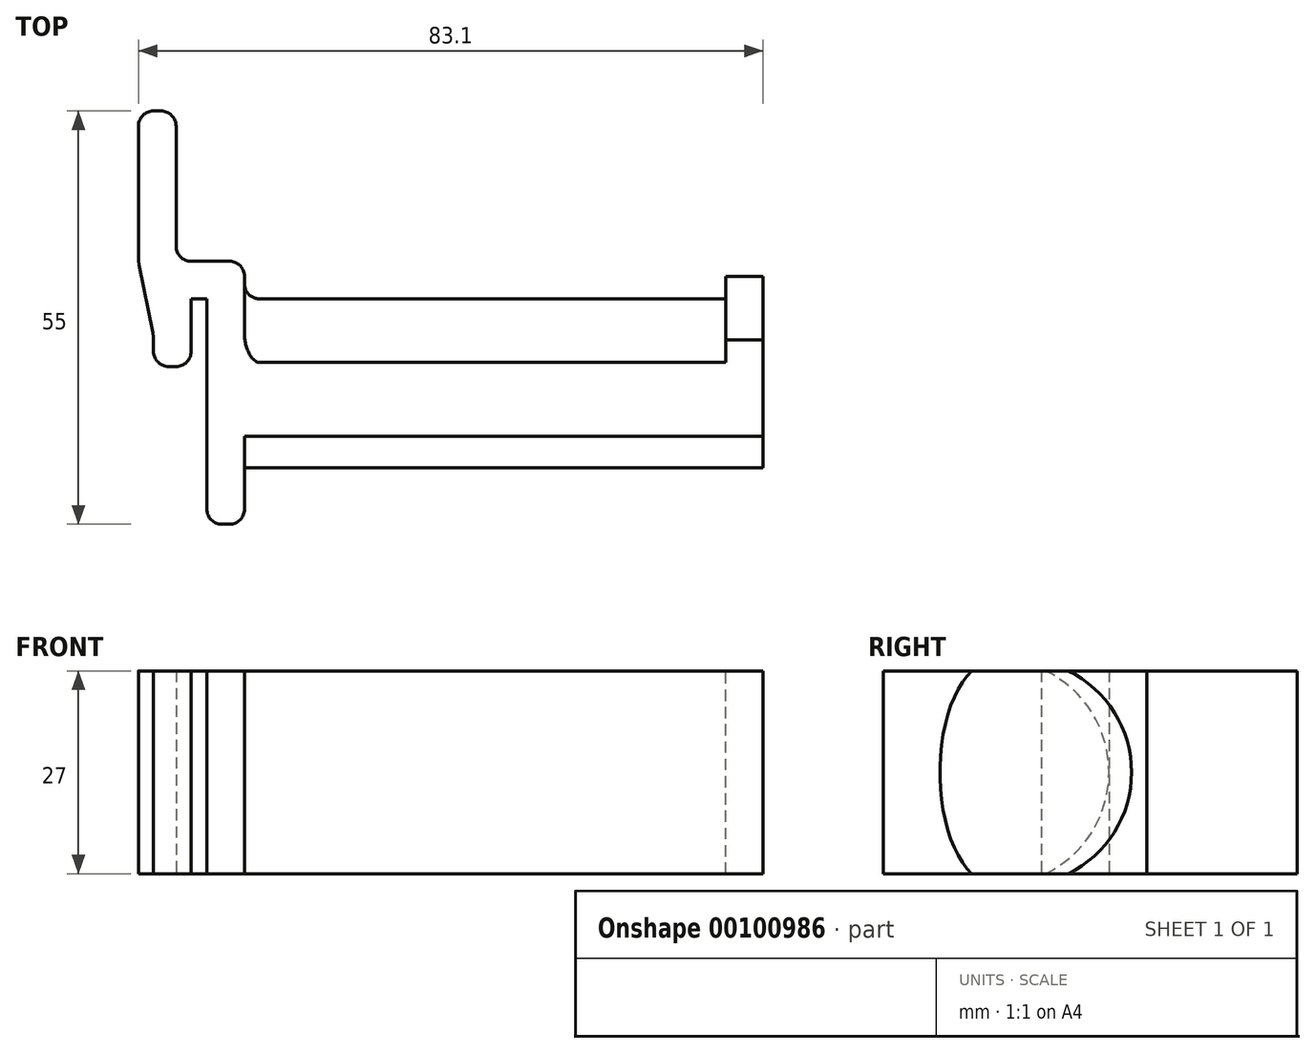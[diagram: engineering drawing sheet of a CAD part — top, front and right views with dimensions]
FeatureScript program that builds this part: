
annotation { "Feature Type Name" : "Feature", "Feature Type Description" : "" }
export const myFeature = defineFeature(function(context is Context, id is Id, definition is map)
    precondition{}
    {
        {
            assignVariable(context, id + "F0", {"name" : "Diameter", "anyValue" : 30});
        }
        {
            assignVariable(context, id + "F1", {"name" : "Width", "anyValue" : 62});
        }
        {
            var Q0;
            Q0=qCreatedBy(makeId("Top.planeOp"),FACE);
            var sketch = newSketch(context, id + "F2", { "sketchPlane" : qUnion([Q0])});
            skLineSegment(sketch, "E0", {"start": v(-10.1, -14) * mm, "end": v(-9.1, -14) * mm});
            skLineSegment(sketch, "E1", {"start": v(-7.1, -12) * mm, "end": v(-7.1, -5) * mm});
            skLineSegment(sketch, "E2", {"start": v(-7.1, -5) * mm, "end": v(-5, -5) * mm});
            skLineSegment(sketch, "E3", {"start": v(-5, -5) * mm, "end": v(-5, -33) * mm});
            skLineSegment(sketch, "E4", {"start": v(-3, -35) * mm, "end": v(-2, -35) * mm});
            skLineSegment(sketch, "E5", {"start": v(0, -33) * mm, "end": v(0, -2) * mm});
            skLineSegment(sketch, "E6", {"start": v(-2, 0) * mm, "end": v(-7.1, 0) * mm});
            skLineSegment(sketch, "E7", {"start": v(-9.1, 2) * mm, "end": v(-9.1, 18) * mm});
            skLineSegment(sketch, "E8", {"start": v(-11.1, 20) * mm, "end": v(-12.1, 20) * mm});
            skLineSegment(sketch, "E9", {"start": v(-14.1, 18) * mm, "end": v(-14.1, 0.5) * mm});
            skLineSegment(sketch, "E10", {"start": v(-12.1, -10.5) * mm, "end": v(-12.1, -12) * mm});
            skPoint(sketch, "E11.visualSharp", {"position": v(-9.1, 0) * mm});
            skArc(sketch, "E11.filletArc", {"start": v(-9.1, 2) * mm, "mid": v(-8.51, 0.59) * mm, "end": v(-7.1, 0) * mm});
            skPoint(sketch, "E12.visualSharp", {"position": v(0, 0) * mm});
            skArc(sketch, "E12.filletArc", {"start": v(0, -2) * mm, "mid": v(-0.59, -0.59) * mm, "end": v(-2, 0) * mm});
            skPoint(sketch, "E13.visualSharp", {"position": v(-9.1, 20) * mm});
            skArc(sketch, "E13.filletArc", {"start": v(-9.1, 18) * mm, "mid": v(-9.69, 19.41) * mm, "end": v(-11.1, 20) * mm});
            skPoint(sketch, "E14.visualSharp", {"position": v(-14.1, 20) * mm});
            skArc(sketch, "E14.filletArc", {"start": v(-12.1, 20) * mm, "mid": v(-13.51, 19.41) * mm, "end": v(-14.1, 18) * mm});
            skPoint(sketch, "E15.visualSharp", {"position": v(0, -35) * mm});
            skArc(sketch, "E15.filletArc", {"start": v(-2, -35) * mm, "mid": v(-0.59, -34.41) * mm, "end": v(0, -33) * mm});
            skPoint(sketch, "E16.visualSharp", {"position": v(-5, -35) * mm});
            skArc(sketch, "E16.filletArc", {"start": v(-5, -33) * mm, "mid": v(-4.41, -34.41) * mm, "end": v(-3, -35) * mm});
            skPoint(sketch, "E17.visualSharp", {"position": v(-7.1, -14) * mm});
            skArc(sketch, "E17.filletArc", {"start": v(-9.1, -14) * mm, "mid": v(-7.69, -13.41) * mm, "end": v(-7.1, -12) * mm});
            skPoint(sketch, "E18.visualSharp", {"position": v(-12.1, -14) * mm});
            skArc(sketch, "E18.filletArc", {"start": v(-12.1, -12) * mm, "mid": v(-11.51, -13.41) * mm, "end": v(-10.1, -14) * mm});
            skLineSegment(sketch, "E19", {"start": v(-14, -0.49) * mm, "end": v(-12.2, -9.51) * mm});
            skPoint(sketch, "E20", {"position": v(-13.1, -5) * mm});
            skPoint(sketch, "E21.visualSharp", {"position": v(-14.1, 0) * mm});
            skArc(sketch, "E21.filletArc", {"start": v(-14.1, 0.5) * mm, "mid": v(-14.08, 0) * mm, "end": v(-14, -0.49) * mm});
            skPoint(sketch, "E22.visualSharp", {"position": v(-12.1, -10) * mm});
            skArc(sketch, "E22.filletArc", {"start": v(-12.1, -10.5) * mm, "mid": v(-12.12, -10) * mm, "end": v(-12.2, -9.51) * mm});
            skSolve(sketch);
        }
        {
            var Q0;
            Q0=qSketchRegion(id+"F2",true);
            extrude(context, id + "F3", {"entities" : qUnion([Q0]), "endBound" : BoundingType.SYMMETRIC, "depth" : (getVariable(context, 'Diameter') * 0.9) * mm});
        }
        {
            var Q0;
            Q0=makeQuery(id+"F3.opExtrude","SWEPT_FACE",FACE,{"disambiguationData":[OSD([sQuery(id+"F2.wireOp",EDGE,"E5")])]});
            var sketch = newSketch(context, id + "F4", { "sketchPlane" : qUnion([Q0])});
            skArc(sketch, "E23", {"start": v(-13.46, -13.5) * mm, "mid": v(-5, 0) * mm, "end": v(-13.46, 13.5) * mm});
            skEllipse(sketch, "E24", {"center": v(-20, 0) * mm, "majorRadius": 15 * mm, "minorRadius": 7.5 * mm, "majorAxis": v(0, -1)});
            skLineSegment(sketch, "E25", {"start": v(-13.46, 13.5) * mm, "end": v(-23.27, 13.5) * mm});
            skLineSegment(sketch, "E26", {"start": v(-13.46, -13.5) * mm, "end": v(-23.27, -13.5) * mm});
            skSolve(sketch);
        }
        {
            var Q0;
            {var subQ0=sQuery(id+"F4.wireOp",EDGE,"E25");var subQ1=sQuery(id+"F4.wireOp",EDGE,"E24");var subQ2=makeQuery(id+"F4.imprint","INTERSECT",VERTEX,{"derivedFrom":[subQ1,subQ0]});Q0=makeQuery(id+"F4.imprint","IMPRINT",FACE,{"disambiguationData":[TD([[makeQuery(id+"F4.imprint","IMPRINT",EDGE,{"disambiguationData":[TD([[subQ2,1.0]])],"derivedFrom":subQ1}),1.0]])]});}
            var Q1;
            {var subQ0=sQuery(id+"F4.wireOp",EDGE,"E23");Q1=makeQuery(id+"F4.imprint","IMPRINT",FACE,{"disambiguationData":[TD([[makeQuery(id+"F4.imprint","IMPRINT",EDGE,{"derivedFrom":subQ0}),1.0]])]});}
            extrude(context, id + "F5", {"entities" : qUnion([Q0, Q1]), "operationType" : NewBodyOperationType.ADD, "depth" : (getVariable(context, 'Width') + 7) * mm});
        }
        {
            var Q0;
            Q0=makeQuery(id+"F5.opExtrude","CAP_FACE",FACE,{"disambiguationData":[OSD([sQuery(id+"F4.wireOp",EDGE,"E23"),sQuery(id+"F4.wireOp",EDGE,"E24"),sQuery(id+"F4.wireOp",EDGE,"E25"),sQuery(id+"F4.wireOp",EDGE,"E26")])],"isStart":false});
            var sketch = newSketch(context, id + "F6", { "sketchPlane" : qUnion([Q0])});
            skLineSegment(sketch, "E27.0", {"start": v(-13.46, 13.5) * mm, "end": v(-2, 13.5) * mm});
            skLineSegment(sketch, "E28.0", {"start": v(-13.46, -13.5) * mm, "end": v(-2, -13.5) * mm});
            skArc(sketch, "E29", {"start": v(-10.46, -13.5) * mm, "mid": v(-2, 0) * mm, "end": v(-10.46, 13.5) * mm});
            skPoint(sketch, "E30", {"position": v(-20, 0) * mm});
            skSolve(sketch);
        }
        {
            var Q0;
            Q0=qSketchRegion(id+"F6",true);
            var Q1;
            {var subQ2=sQuery(id+"F6.wireOp",EDGE,"E29");Q1=makeQuery(id+"F6.imprint","IMPRINT",FACE,{"disambiguationData":[TD([[makeQuery(id+"F6.imprint","IMPRINT",EDGE,{"derivedFrom":subQ2}),1.0]])]});}
            extrude(context, id + "F7", {"entities" : qUnion([Q0, Q1]), "operationType" : NewBodyOperationType.ADD, "oppositeDirection" : true, "depth" : 5 * mm});
        }
        {
            var Q0;
            Q0=makeQuery(id+"F5.opExtrude","CAP_EDGE",EDGE,{"disambiguationData":[OSD([sQuery(id+"F4.wireOp",EDGE,"E23")])],"isStart":true});
            var Q1;
            Q1=makeQuery(id+"F5.opExtrude","CAP_EDGE",EDGE,{"disambiguationData":[OSD([sQuery(id+"F4.wireOp",EDGE,"E24")])],"isStart":true});
            var Q2;
            Q2=makeQuery(id+"F7.opExtrude","CAP_EDGE",EDGE,{"disambiguationData":[OSD([sQuery(id+"F4.wireOp",EDGE,"E23")])],"isStart":false});
            fillet(context, id + "F8", {"entities" : qUnion([Q0, Q1, Q2]), "radius" : 2 * mm, "tangentPropagation" : true, "allowEdgeOverflow" : false});
        }
    });
